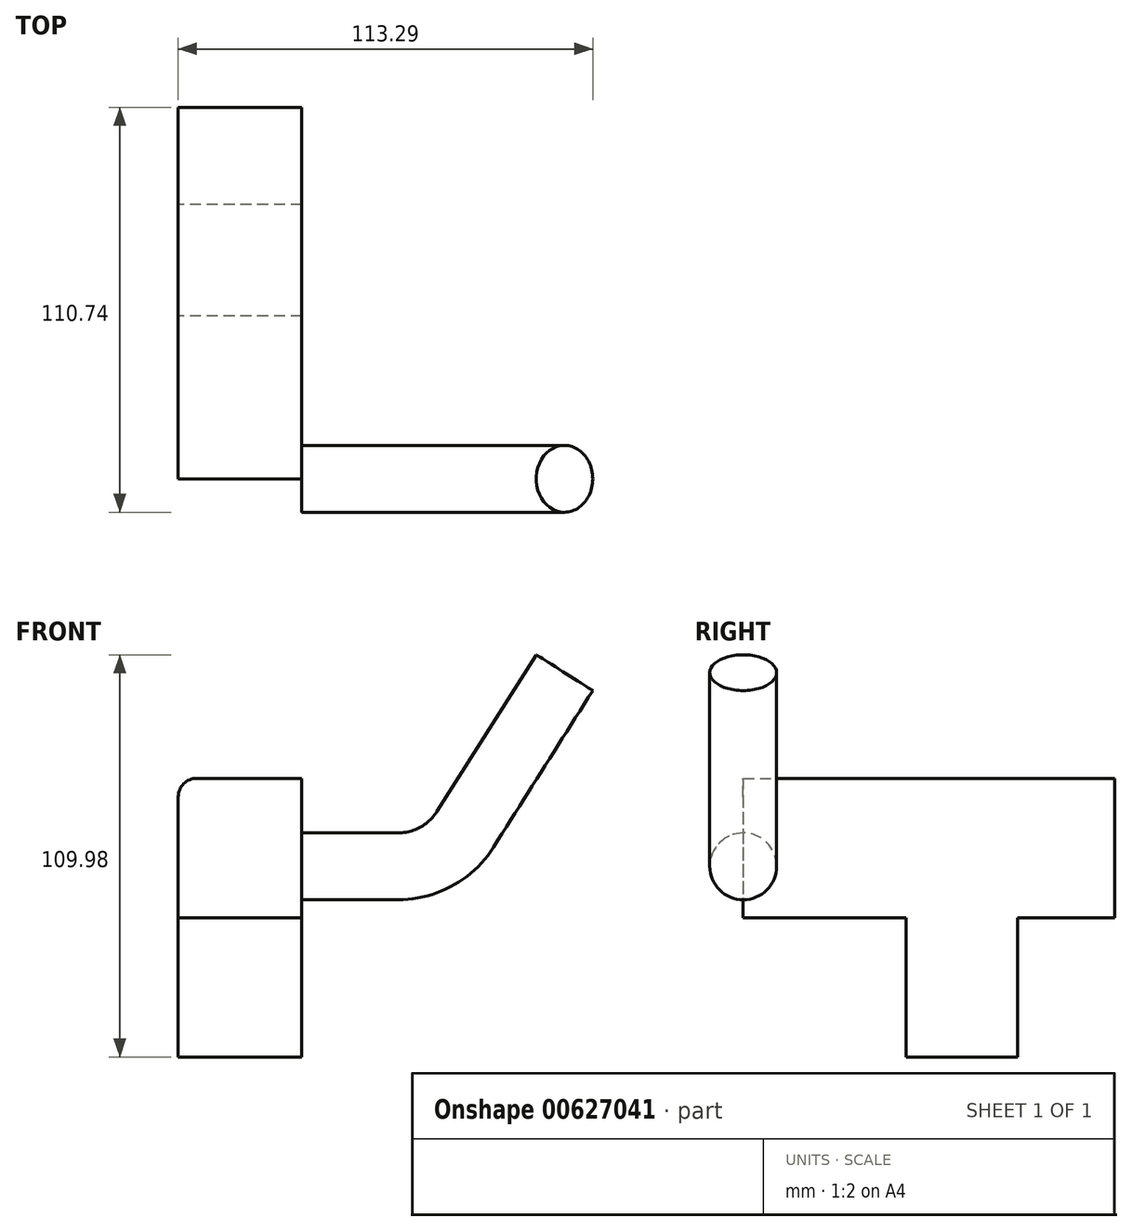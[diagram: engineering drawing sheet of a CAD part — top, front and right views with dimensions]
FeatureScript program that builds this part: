
annotation { "Feature Type Name" : "Feature", "Feature Type Description" : "" }
export const myFeature = defineFeature(function(context is Context, id is Id, definition is map)
    precondition{}
    {
        {
            var Q0;
            Q0=qCreatedBy(makeId("Right.planeOp"),FACE);
            var sketch = newSketch(context, id + "F0", { "sketchPlane" : qUnion([Q0])});
            skLineSegment(sketch, "E0.bottom", {"start": v(-65.76, 66.47) * mm, "end": v(35.84, 66.47) * mm});
            skLineSegment(sketch, "E0.top", {"start": v(-65.76, 28.37) * mm, "end": v(35.84, 28.37) * mm});
            skLineSegment(sketch, "E0.left", {"start": v(-65.76, 66.47) * mm, "end": v(-65.76, 28.37) * mm});
            skLineSegment(sketch, "E0.right", {"start": v(35.84, 66.47) * mm, "end": v(35.84, 28.37) * mm});
            skLineSegment(sketch, "E1.bottom", {"start": v(-21.22, 45.22) * mm, "end": v(9.26, 45.22) * mm});
            skLineSegment(sketch, "E1.top", {"start": v(-21.22, -9.73) * mm, "end": v(9.26, -9.73) * mm});
            skLineSegment(sketch, "E1.left", {"start": v(-21.22, 45.22) * mm, "end": v(-21.22, -9.73) * mm});
            skLineSegment(sketch, "E1.right", {"start": v(9.26, 45.22) * mm, "end": v(9.26, -9.73) * mm});
            skSolve(sketch);
        }
        {
            var Q0;
            Q0 = qSketchRegion(id + "F0", true);
            extrude(context, id + "F1", {"entities" : qUnion([Q0]), "depth" : 33.78 * mm, "offsetDistance" : 25.4 * mm});
        }
        {
            var Q0;
            Q0=makeQuery(id+"F1.opExtrude","CAP_EDGE",EDGE,{"disambiguationData":[OSD([sQuery(id+"F0.wireOp",EDGE,"E0.bottom")])],"isStart":true});
            fillet(context, id + "F2", {"entities" : qUnion([Q0]), "radius" : 5.08 * mm, "tangentPropagation" : true, "allowEdgeOverflow" : false});
        }
        {
            var Q0;
            Q0=makeQuery(id+"F1.opExtrude","CAP_FACE",FACE,{"disambiguationData":[OSD([sQuery(id+"F0.wireOp",EDGE,"E0.bottom"),sQuery(id+"F0.wireOp",EDGE,"E0.top"),sQuery(id+"F0.wireOp",EDGE,"E0.left"),sQuery(id+"F0.wireOp",EDGE,"E0.right"),sQuery(id+"F0.wireOp",EDGE,"E1.top"),sQuery(id+"F0.wireOp",EDGE,"E1.left"),sQuery(id+"F0.wireOp",EDGE,"E1.right")])],"isStart":false});
            var sketch = newSketch(context, id + "F3", { "sketchPlane" : qUnion([Q0])});
            skCircle(sketch, "E2", {"center": v(-65.76, 42.4) * mm, "radius": 9.14 * mm});
            skSolve(sketch);
        }
        {
            var Q0;
            Q0=makeQuery(id+"F1.opExtrude","SWEPT_FACE",FACE,{"disambiguationData":[OSD([sQuery(id+"F0.wireOp",EDGE,"E0.left")])]});
            var sketch = newSketch(context, id + "F4", { "sketchPlane" : qUnion([Q0])});
            skLineSegment(sketch, "E3", {"start": v(33.78, 42.09) * mm, "end": v(60.05, 42.09) * mm});
            skArc(sketch, "E4", {"start": v(60.05, 42.09) * mm, "mid": v(70.68, 44.82) * mm, "end": v(78.68, 52.34) * mm});
            skLineSegment(sketch, "E5", {"start": v(78.68, 52.34) * mm, "end": v(105.83, 95.2) * mm});
            skSolve(sketch);
        }
        {
            var Q0;
            {var subQ0=sQuery(id+"F3.wireOp",EDGE,"E2");var subQ1=makeQuery(id+"F1.opExtrude","CAP_EDGE",EDGE,{"disambiguationData":[OSD([sQuery(id+"F0.wireOp",EDGE,"E0.left")])],"isStart":false});var subQ2=makeQuery(id+"F3.imprint","INTERSECT",VERTEX,{"disambiguationData":[OD(0.0)],"derivedFrom":[subQ1,subQ0]});Q0=makeQuery(id+"F3.imprint","IMPRINT",FACE,{"disambiguationData":[TD([[makeQuery(id+"F3.imprint","IMPRINT",EDGE,{"disambiguationData":[TD([[subQ2,-1.0]])],"derivedFrom":subQ0}),1.0]])]});}
            var Q1;
            {var subQ0=sQuery(id+"F3.wireOp",EDGE,"E2");var subQ1=makeQuery(id+"F1.opExtrude","CAP_EDGE",EDGE,{"disambiguationData":[OSD([sQuery(id+"F0.wireOp",EDGE,"E0.left")])],"isStart":false});var subQ2=makeQuery(id+"F3.imprint","INTERSECT",VERTEX,{"disambiguationData":[OD(0.0)],"derivedFrom":[subQ1,subQ0]});Q1=makeQuery(id+"F3.imprint","IMPRINT",FACE,{"disambiguationData":[TD([[makeQuery(id+"F3.imprint","IMPRINT",EDGE,{"disambiguationData":[TD([[subQ2,1.0]])],"derivedFrom":subQ0}),1.0]])]});}
            var Q2;
            Q2=sQuery(id+"F4.wireOp",EDGE,"E3");
            var Q3;
            Q3=sQuery(id+"F4.wireOp",EDGE,"E4");
            var Q4;
            Q4=sQuery(id+"F4.wireOp",EDGE,"E5");
            sweep(context, id + "F5", {"operationType" : NewBodyOperationType.ADD, "profiles" : qUnion([Q0, Q1]), "path" : qUnion([Q2, Q3, Q4])});
        }
    });
